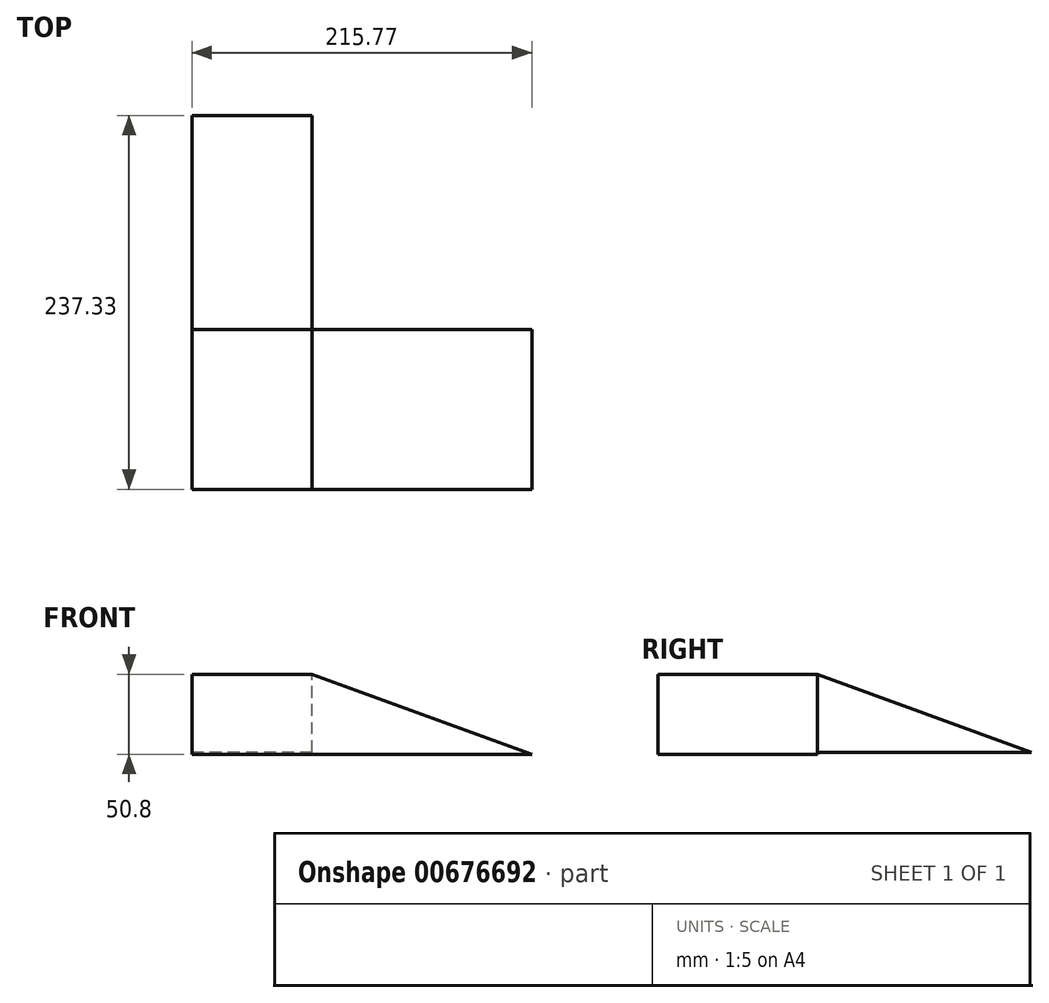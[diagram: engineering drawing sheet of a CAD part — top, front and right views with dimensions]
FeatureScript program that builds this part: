
annotation { "Feature Type Name" : "Feature", "Feature Type Description" : "" }
export const myFeature = defineFeature(function(context is Context, id is Id, definition is map)
    precondition{}
    {
        {
            var Q0;
            Q0=qCreatedBy(makeId("Front.planeOp"),FACE);
            var sketch = newSketch(context, id + "F0", { "sketchPlane" : qUnion([Q0])});
            skLineSegment(sketch, "E0.bottom", {"start": v(38.1, -25.4) * mm, "end": v(-38.1, -25.4) * mm});
            skLineSegment(sketch, "E0.top", {"start": v(38.1, 25.4) * mm, "end": v(-38.1, 25.4) * mm});
            skLineSegment(sketch, "E0.left", {"start": v(38.1, -25.4) * mm, "end": v(38.1, 25.4) * mm});
            skLineSegment(sketch, "E0.right", {"start": v(-38.1, -25.4) * mm, "end": v(-38.1, 25.4) * mm});
            skPoint(sketch, "E0.middle", {"position": v(0, 0) * mm});
            skLineSegment(sketch, "E1", {"start": v(-38.1, 25.4) * mm, "end": v(-38.1, -25.4) * mm});
            skPoint(sketch, "E2", {"position": v(38.1, 25.4) * mm});
            skPoint(sketch, "E3", {"position": v(38.1, -25.4) * mm});
            skPoint(sketch, "E4", {"position": v(-38.1, -25.4) * mm});
            skPoint(sketch, "E5", {"position": v(-38.1, 25.4) * mm});
            skLineSegment(sketch, "E6", {"start": v(-38.1, 25.4) * mm, "end": v(-177.67, -25.4) * mm});
            skLineSegment(sketch, "E7", {"start": v(38.1, 25.4) * mm, "end": v(177.67, -25.4) * mm});
            skLineSegment(sketch, "E8", {"start": v(177.67, -25.4) * mm, "end": v(38.1, -25.4) * mm});
            skLineSegment(sketch, "E9", {"start": v(-38.1, -25.4) * mm, "end": v(-177.67, -25.4) * mm});
            skSolve(sketch);
        }
        {
            var Q0;
            {var subQ0=sQuery(id+"F0.wireOp",EDGE,"E0.bottom");Q0=makeQuery(id+"F0.imprint","IMPRINT",FACE,{"disambiguationData":[TD([[makeQuery(id+"F0.imprint","IMPRINT",EDGE,{"derivedFrom":subQ0}),-1.0]])]});}
            var Q1;
            Q1=makeQuery(id+"F0.imprint","IMPRINT",FACE,{"disambiguationData":[TD([[makeQuery(id+"F0.imprint","IMPRINT",EDGE,{"derivedFrom":sQuery(id+"F0.wireOp",EDGE,"E1")}),-1.0]])]});
            var Q2;
            Q2=makeQuery(id+"F0.imprint","IMPRINT",FACE,{"disambiguationData":[TD([[makeQuery(id+"F0.imprint","IMPRINT",EDGE,{"derivedFrom":sQuery(id+"F0.wireOp",EDGE,"E0.left")}),-1.0]])]});
            extrude(context, id + "F1", {"entities" : qUnion([Q0, Q1, Q2]), "depth" : 101.6 * mm, "offsetDistance" : 25.4 * mm});
        }
        {
            var Q0;
            Q0=qCreatedBy(makeId("Right.planeOp"),FACE);
            var sketch = newSketch(context, id + "F2", { "sketchPlane" : qUnion([Q0])});
            skLineSegment(sketch, "E10", {"start": v(0, 0) * mm, "end": v(0, 25.32) * mm});
            skLineSegment(sketch, "E11", {"start": v(0, 25.32) * mm, "end": v(0, -24.08) * mm});
            skLineSegment(sketch, "E12", {"start": v(0, 25.32) * mm, "end": v(135.73, -24.08) * mm});
            skLineSegment(sketch, "E13", {"start": v(0, -24.08) * mm, "end": v(135.73, -24.08) * mm});
            skSolve(sketch);
        }
        {
            var Q0;
            {var subQ0=sQuery(id+"F2.wireOp",EDGE,"E12");Q0=makeQuery(id+"F2.imprint","IMPRINT",FACE,{"disambiguationData":[TD([[makeQuery(id+"F2.imprint","IMPRINT",EDGE,{"derivedFrom":subQ0}),-1.0]])]});}
            extrude(context, id + "F3", {"entities" : qUnion([Q0]), "operationType" : NewBodyOperationType.ADD, "endBound" : BoundingType.SYMMETRIC, "depth" : 76.2 * mm, "offsetDistance" : 25.4 * mm});
        }
    });
